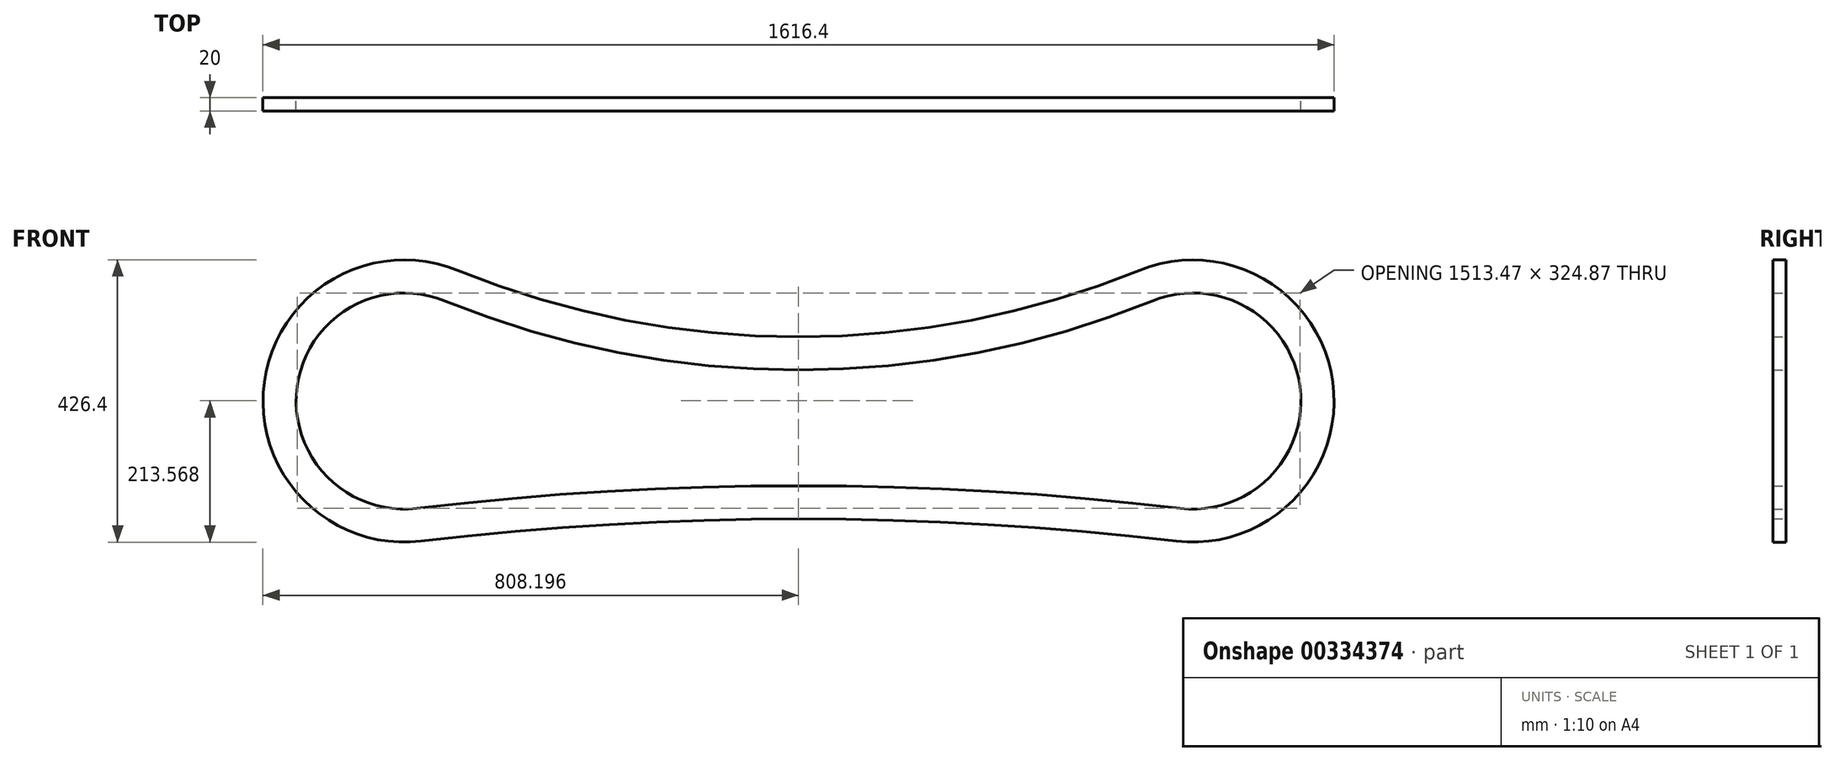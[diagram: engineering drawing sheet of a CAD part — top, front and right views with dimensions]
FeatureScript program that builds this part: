
annotation { "Feature Type Name" : "Feature", "Feature Type Description" : "" }
export const myFeature = defineFeature(function(context is Context, id is Id, definition is map)
    precondition{}
    {
        {
            var Q0;
            Q0=qCreatedBy(makeId("Front.planeOp"),FACE);
            var sketch = newSketch(context, id + "F0", { "sketchPlane" : qUnion([Q0])});
            skArc(sketch, "E0", {"start": v(-512.04, 197.51) * mm, "mid": v(-803.6, 28.51) * mm, "end": v(-567.26, -211.72) * mm});
            skArc(sketch, "E1", {"start": v(572.63, -211.72) * mm, "mid": v(808.97, 28.51) * mm, "end": v(517.41, 197.51) * mm});
            skLineSegment(sketch, "E2", {"start": v(-592.31, 0) * mm, "end": v(597.69, 0) * mm});
            skArc(sketch, "E3", {"start": v(-512.04, 197.51) * mm, "mid": v(2.69, 96.9) * mm, "end": v(517.41, 197.51) * mm});
            skPoint(sketch, "E3.centerSnap0", {"position": v(2.69, 0) * mm});
            skArc(sketch, "E4", {"start": v(572.63, -211.72) * mm, "mid": v(2.69, -178.12) * mm, "end": v(-567.26, -211.72) * mm});
            skArc(sketch, "E5.0", {"start": v(-530.87, 151.19) * mm, "mid": v(-754.05, 21.82) * mm, "end": v(-573.14, -162.07) * mm});
            skArc(sketch, "E6.0", {"start": v(-530.87, 151.19) * mm, "mid": v(2.69, 46.9) * mm, "end": v(536.24, 151.19) * mm});
            skArc(sketch, "E7.0", {"start": v(578.5, -162.07) * mm, "mid": v(759.42, 21.82) * mm, "end": v(536.24, 151.19) * mm});
            skArc(sketch, "E8.0", {"start": v(578.5, -162.07) * mm, "mid": v(2.69, -128.12) * mm, "end": v(-573.14, -162.07) * mm});
            skSolve(sketch);
        }
        {
            var Q0;
            Q0=makeQuery(id+"F0.imprint","IMPRINT",FACE,{"disambiguationData":[TD([[makeQuery(id+"F0.imprint","IMPRINT",EDGE,{"derivedFrom":sQuery(id+"F0.wireOp",EDGE,"E0")}),1.0]])]});
            extrude(context, id + "F1", {"entities" : qUnion([Q0]), "depth" : 20 * mm});
        }
    });
